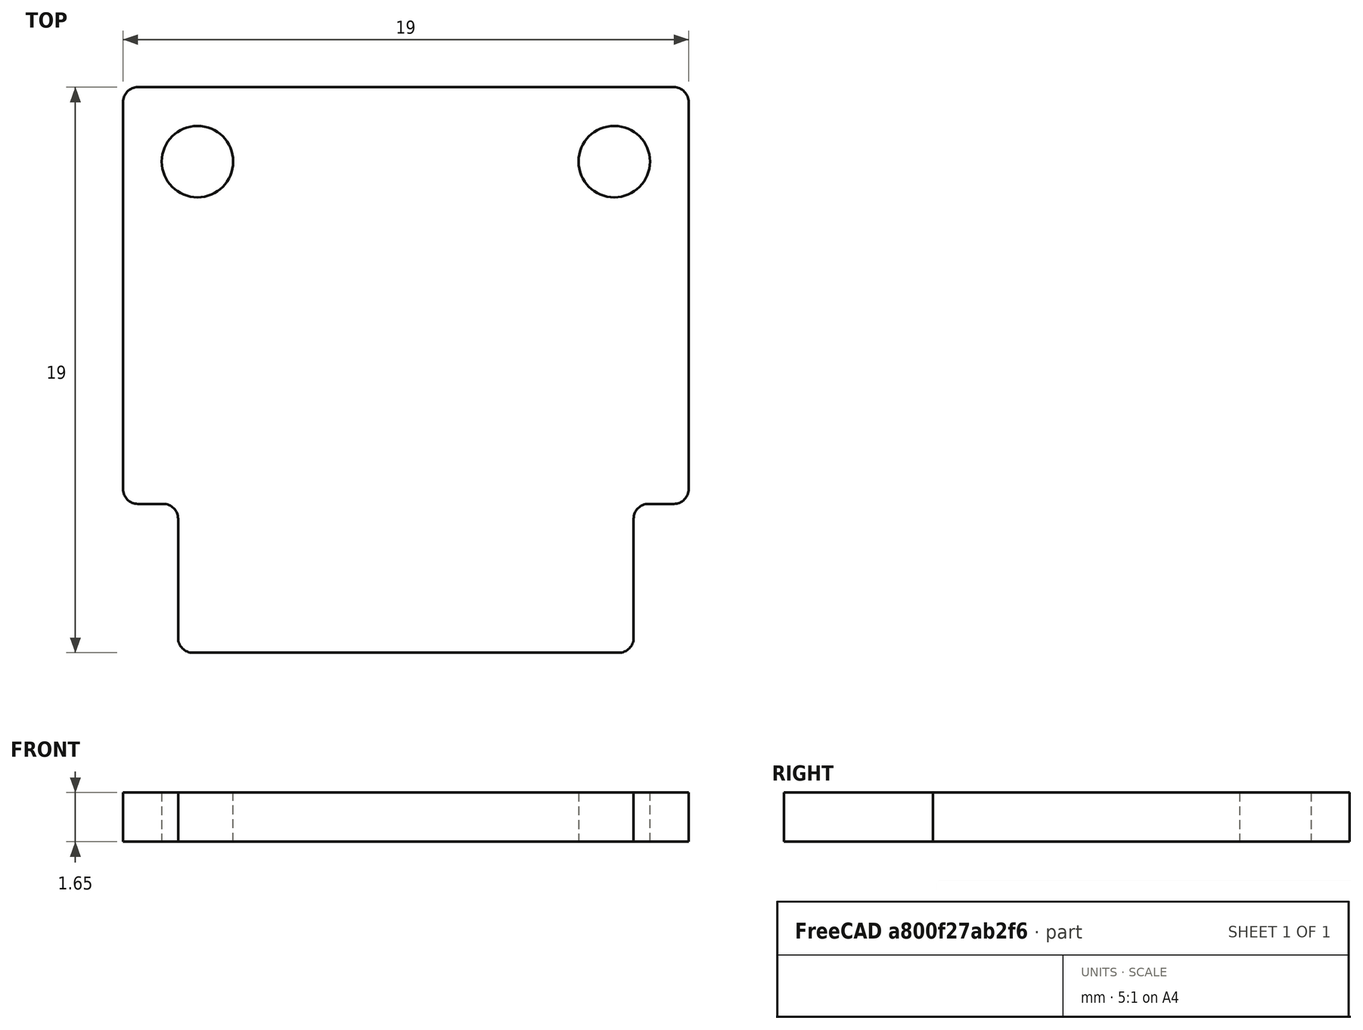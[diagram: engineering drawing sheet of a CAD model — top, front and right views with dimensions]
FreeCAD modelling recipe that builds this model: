
FCSTD DOCUMENT  (FreeCAD 0.20R27078 (Git))
Label: pimoroni_vl53l1x
License: All rights reserved
LicenseURL: http://en.wikipedia.org/wiki/All_rights_reserved
objects: TechDraw::DrawViewDimension×8, Sketcher::SketchObject×1, TechDraw::DrawSVGTemplate×1, TechDraw::DrawViewSymbol×1, PartDesign::Pad×1, PartDesign::Body×1, TechDraw::DrawProjGroupItem×1, TechDraw::DrawProjGroup×1, TechDraw::DrawPage×1
note: 4 computed .brp shape members not serialized (recipe doc carries the construction recipe); baked Part::Feature solids carry a one-line shape summary decoded from their .brp

FEATURE [Sketcher::SketchObject] Sketch
  FullyConstrained = true
  MapMode = 5
  Support = -> [XY_Plane]
  sketch-geometry (18):
    g0: LineSegment StartX=-9 StartY=6.5 StartZ=0 EndX=9 EndY=6.5 EndZ=0
    g1: LineSegment StartX=9.5 StartY=6 StartZ=0 EndX=9.5 EndY=-7 EndZ=0
    g2: LineSegment StartX=9 StartY=-7.5 StartZ=0 EndX=8.15 EndY=-7.5 EndZ=0
    g3: LineSegment StartX=-9.5 StartY=-7 StartZ=0 EndX=-9.5 EndY=6 EndZ=0
    g4: ArcOfCircle CenterX=-9 CenterY=6 CenterZ=0 NormalX=0 NormalY=0 NormalZ=1 AngleXU=0 Radius=0.5 StartAngle=1.5708 EndAngle=3.14159
    g5: ArcOfCircle CenterX=9 CenterY=6 CenterZ=0 NormalX=0 NormalY=0 NormalZ=1 AngleXU=0 Radius=0.5 StartAngle=0 EndAngle=1.5708
    g6: LineSegment StartX=7.65 StartY=-8 StartZ=0 EndX=7.65 EndY=-12 EndZ=0
    g7: LineSegment StartX=7.15 StartY=-12.5 StartZ=0 EndX=-7.15 EndY=-12.5 EndZ=0
    g8: LineSegment StartX=-7.65 StartY=-12 StartZ=0 EndX=-7.65 EndY=-8 EndZ=0
    g9: LineSegment StartX=-8.15 StartY=-7.5 StartZ=0 EndX=-9 EndY=-7.5 EndZ=0
    g10: ArcOfCircle CenterX=-9 CenterY=-7 CenterZ=0 NormalX=0 NormalY=0 NormalZ=1 AngleXU=0 Radius=0.5 StartAngle=3.14159 EndAngle=4.71239
    g11: ArcOfCircle CenterX=9 CenterY=-7 CenterZ=0 NormalX=0 NormalY=0 NormalZ=1 AngleXU=0 Radius=0.5 StartAngle=4.71239 EndAngle=6.28319
    g12: ArcOfCircle CenterX=7.15 CenterY=-12 CenterZ=0 NormalX=0 NormalY=0 NormalZ=1 AngleXU=0 Radius=0.5 StartAngle=4.71239 EndAngle=6.28319
    g13: ArcOfCircle CenterX=-7.15 CenterY=-12 CenterZ=0 NormalX=0 NormalY=0 NormalZ=1 AngleXU=0 Radius=0.5 StartAngle=3.14159 EndAngle=4.71239
    g14: Circle CenterX=-7 CenterY=4 CenterZ=0 NormalX=0 NormalY=0 NormalZ=1 AngleXU=0 Radius=1.2
    g15: Circle CenterX=7 CenterY=4 CenterZ=0 NormalX=0 NormalY=0 NormalZ=1 AngleXU=0 Radius=1.2
    g16: ArcOfCircle CenterX=-8.15 CenterY=-8 CenterZ=0 NormalX=0 NormalY=0 NormalZ=1 AngleXU=0 Radius=0.5 StartAngle=0 EndAngle=1.5708
    g17: ArcOfCircle CenterX=8.15 CenterY=-8 CenterZ=0 NormalX=0 NormalY=0 NormalZ=1 AngleXU=0 Radius=0.5 StartAngle=1.5708 EndAngle=3.14159
  constraints (41):
    c: Horizontal(g2)
    c: Vertical(g1)
    c: Tangent(g0,g4) = 1.5708
    c: Tangent(g3,g4) = 1.5708
    c: Tangent(g0,g5) = 1.5708
    c: Tangent(g1,g5) = 1.5708
    c: Horizontal(g7)
    c: Vertical(g6)
    c: Vertical(g8)
    c: Tangent(g3,g10) = 1.5708
    c: Tangent(g9,g10) = 1.5708
    c: Tangent(g2,g11) = 1.5708
    c: Tangent(g1,g11) = 1.5708
    c: Tangent(g6,g12) = 1.5708
    c: Tangent(g7,g12) = 1.5708
    c: Tangent(g7,g13) = 1.5708
    c: Tangent(g8,g13) = 1.5708
    c: Tangent(g2,g9)
    c: Symmetric(g10,g11,g-2)
    c: Symmetric(g12,g13,g-2)
    c: Equal(g5,g4)
    c: Diameter(g4) = 1
    c: Diameter(g10) = 1
    c: Diameter(g13) = 1
    c: DistanceX(g8,g6) = 15.3
    c: DistanceX(g3,g1) = 19
    c: Equal(g15,g14)
    c: Symmetric(g15,g14,g-2)
    c: Symmetric(g0,g0,g-2)
    c: DistanceY(g-1,g3) = 6
    c: Diameter(g14) = 2.4
    c: DistanceX(g3,g14) = 2.5
    c: DistanceY(g14,g0) = 2.5
    c: Tangent(g9,g16) = -1.5708
    c: Tangent(g8,g16) = -1.5708
    c: Tangent(g2,g17) = -1.5708
    c: Tangent(g6,g17) = -1.5708
    c: Equal(g17,g11)
    c: Equal(g16,g17)
    c: DistanceY(g7,g0) = 19
    c: DistanceY(g7,g2) = 5
FEATURE [TechDraw::DrawSVGTemplate] Template
  EditableTexts = Designed_by_Name=Designed by Name; Drawing_number=Drawing number; FC-Date=Date; FC-SC=Scale; FC-SH=Sheet; FC-Title=Title; Subtitle=Subtitle; Weight=Weight
  Height = 210
  Orientation = 1
  Width = 297
FEATURE [TechDraw::DrawViewSymbol] ActiveView
  LockPosition = false
  Rotation = 0
  ScaleType = 2
  Symbol = <blob: 12767 chars omitted>
  X = 155.842
  Y = 88.9687
FEATURE [PartDesign::Pad] Pad
  Direction = (0,0,1)
  Length = 1.65
  Length2 = 100
  Profile = -> Sketch
  ReferenceAxis = -> Sketch [N_Axis]
  Type = 0
FEATURE [PartDesign::Body] Body  label="BreakoutGardenVL53L1x"
  Group = -> [Sketch,Pad]
  Origin = -> Origin
  Tip = -> Pad
FEATURE [TechDraw::DrawProjGroupItem] ProjItem  label="Front"
  CoarseView = false
  Direction = (0,0,1)
  Focus = 100
  HardHidden = false
  IsoCount = 0
  IsoHidden = false
  IsoVisible = false
  LockPosition = true
  Perspective = false
  Rotation = 0
  RotationVector = (1,0,0)
  Scale = 4
  ScaleType = 2
  SeamHidden = false
  SeamVisible = true
  SmoothHidden = false
  SmoothVisible = true
  Source = -> [Body]
  Type = 0
  X = 0
  XDirection = (1,0,0)
  Y = 0
FEATURE [TechDraw::DrawProjGroup] ProjGroup
  Anchor = -> ProjItem
  AutoDistribute = true
  LockPosition = false
  ProjectionType = 0
  Rotation = 0
  Scale = 4
  ScaleType = 1
  Source = -> [Body]
  Views = -> [ProjItem]
  X = 94.0768
  Y = 141.721
  spacingX = 15
  spacingY = 15
FEATURE [TechDraw::DrawViewDimension] Dimension
  Arbitrary = false
  ArbitraryTolerances = false
  EqualTolerance = true
  FormatSpec = %.2f
  FormatSpecOverTolerance = %+.2f
  FormatSpecUnderTolerance = %+.2f
  Inverted = false
  LockPosition = false
  MeasureType = 1
  OverTolerance = 0
  References2D = -> [ProjItem]
  Rotation = 0
  ScaleType = 0
  TheoreticalExact = false
  Type = 1
  UnderTolerance = 0
  X = 2.44384
  Y = -53.0693
FEATURE [TechDraw::DrawViewDimension] Dimension001
  Arbitrary = false
  ArbitraryTolerances = false
  EqualTolerance = true
  FormatSpec = %.2f
  FormatSpecOverTolerance = %+.2f
  FormatSpecUnderTolerance = %+.2f
  Inverted = false
  LockPosition = false
  MeasureType = 1
  OverTolerance = 0
  References2D = -> [ProjItem]
  Rotation = 0
  ScaleType = 0
  TheoreticalExact = false
  Type = 2
  UnderTolerance = 0
  X = -61.3194
  Y = -28
FEATURE [TechDraw::DrawViewDimension] Dimension002
  Arbitrary = false
  ArbitraryTolerances = false
  EqualTolerance = true
  FormatSpec = %.2f
  FormatSpecOverTolerance = %+.2f
  FormatSpecUnderTolerance = %+.2f
  Inverted = false
  LockPosition = false
  MeasureType = 1
  OverTolerance = 0
  References2D = -> [ProjItem]
  Rotation = 0
  ScaleType = 0
  TheoreticalExact = false
  Type = 2
  UnderTolerance = 0
  X = -54.3194
  Y = 10.6
FEATURE [TechDraw::DrawViewDimension] Dimension003
  Arbitrary = false
  ArbitraryTolerances = false
  EqualTolerance = true
  FormatSpec = ⌀%.2f
  FormatSpecOverTolerance = %+.2f
  FormatSpecUnderTolerance = %+.2f
  Inverted = false
  LockPosition = false
  MeasureType = 1
  OverTolerance = 0
  References2D = -> [ProjItem]
  Rotation = 0
  ScaleType = 0
  TheoreticalExact = false
  Type = 5
  UnderTolerance = 0
  X = -19.1257
  Y = 22.5258
FEATURE [TechDraw::DrawViewDimension] Dimension006
  Arbitrary = false
  ArbitraryTolerances = false
  EqualTolerance = true
  FormatSpec = %.2f
  FormatSpecOverTolerance = %+.2f
  FormatSpecUnderTolerance = %+.2f
  Inverted = false
  LockPosition = false
  MeasureType = 1
  OverTolerance = 0
  References2D = -> [ProjItem]
  Rotation = 0
  ScaleType = 0
  TheoreticalExact = false
  Type = 1
  UnderTolerance = 0
  X = 2.23133
  Y = -73.5208
FEATURE [TechDraw::DrawViewDimension] Dimension007
  Arbitrary = false
  ArbitraryTolerances = false
  EqualTolerance = true
  FormatSpec = %.2f
  FormatSpecOverTolerance = %+.2f
  FormatSpecUnderTolerance = %+.2f
  Inverted = false
  LockPosition = false
  MeasureType = 1
  OverTolerance = 0
  References2D = -> [ProjItem]
  Rotation = 0
  ScaleType = 0
  TheoreticalExact = false
  Type = 2
  UnderTolerance = 0
  X = 12.0617
  Y = 32.15
FEATURE [TechDraw::DrawViewDimension] Dimension008
  Arbitrary = false
  ArbitraryTolerances = false
  EqualTolerance = true
  FormatSpec = %.2f
  FormatSpecOverTolerance = %+.2f
  FormatSpecUnderTolerance = %+.2f
  Inverted = false
  LockPosition = false
  MeasureType = 1
  OverTolerance = 0
  References2D = -> [ProjItem]
  Rotation = 0
  ScaleType = 0
  TheoreticalExact = false
  Type = 1
  UnderTolerance = 0
  X = 13.2368
  Y = 13.3367
FEATURE [TechDraw::DrawViewDimension] Dimension009
  Arbitrary = false
  ArbitraryTolerances = false
  EqualTolerance = true
  FormatSpec = %.2f
  FormatSpecOverTolerance = %+.2f
  FormatSpecUnderTolerance = %+.2f
  Inverted = false
  LockPosition = false
  MeasureType = 1
  OverTolerance = 0
  References2D = -> [ProjItem]
  Rotation = 0
  ScaleType = 0
  TheoreticalExact = false
  Type = 1
  UnderTolerance = 0
  X = 2.86885
  Y = 56.2633
FEATURE [TechDraw::DrawPage] Page
  KeepUpdated = true
  NextBalloonIndex = 1
  ProjectionType = 0
  Template = -> Template
  Views = -> [ActiveView,ProjGroup,Dimension,Dimension001,Dimension002,Dimension003,Dimension006,Dimension007,Dimension008,Dimension009]
